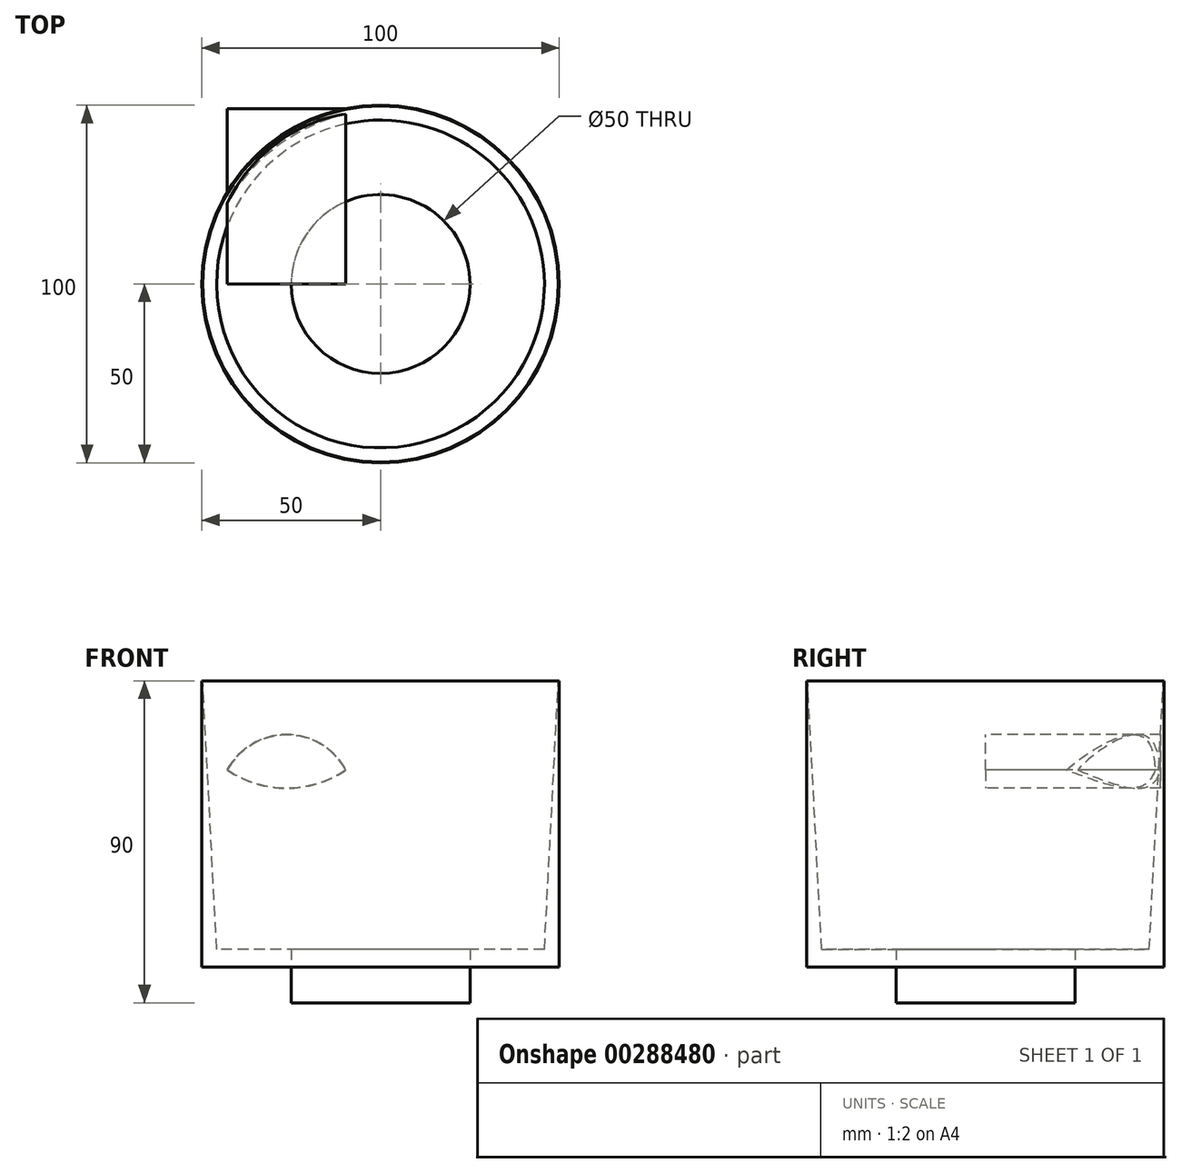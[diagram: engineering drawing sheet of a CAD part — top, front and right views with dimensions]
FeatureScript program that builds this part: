
annotation { "Feature Type Name" : "Feature", "Feature Type Description" : "" }
export const myFeature = defineFeature(function(context is Context, id is Id, definition is map)
    precondition{}
    {
        {
            var Q0;
            Q0=qCreatedBy(makeId("Top.planeOp"),FACE);
            var sketch = newSketch(context, id + "F0", { "sketchPlane" : qUnion([Q0])});
            skCircle(sketch, "E0", {"center": v(0, 0) * mm, "radius": 25 * mm});
            skSolve(sketch);
        }
        {
            var Q0;
            Q0=makeQuery(id+"F0.imprint","IMPRINT",FACE,{"disambiguationData":[TD([[makeQuery(id+"F0.imprint","IMPRINT",EDGE,{"derivedFrom":sQuery(id+"F0.wireOp",EDGE,"E0")}),1.0]])]});
            extrude(context, id + "F1", {"entities" : qUnion([Q0]), "depth" : 10 * mm});
        }
        {
            var Q0;
            Q0=makeQuery(id+"F1.opExtrude","CAP_FACE",FACE,{"disambiguationData":[OSD([sQuery(id+"F0.wireOp",EDGE,"E0")])],"isStart":false});
            var sketch = newSketch(context, id + "F2", { "sketchPlane" : qUnion([Q0])});
            skCircle(sketch, "E1", {"center": v(0, 0) * mm, "radius": 50 * mm});
            skSolve(sketch);
        }
        {
            var Q0;
            Q0=makeQuery(id+"F2.imprint","IMPRINT",FACE,{"disambiguationData":[TD([[makeQuery(id+"F2.imprint","IMPRINT",EDGE,{"derivedFrom":sQuery(id+"F2.wireOp",EDGE,"E1")}),1.0]])]});
            extrude(context, id + "F3", {"entities" : qUnion([Q0]), "depth" : 80 * mm});
        }
        {
            var Q0;
            Q0=makeQuery(id+"F3.opExtrude","CAP_FACE",FACE,{"disambiguationData":[OSD([sQuery(id+"F0.wireOp",EDGE,"E0"),sQuery(id+"F2.wireOp",EDGE,"E1")])],"isStart":false});
            var sketch = newSketch(context, id + "F4", { "sketchPlane" : qUnion([Q0])});
            skCircle(sketch, "E2", {"center": v(0, 0) * mm, "radius": 49.75 * mm});
            skSolve(sketch);
        }
        {
            var Q0;
            Q0 = qSketchRegion(id + "F4", true);
            extrude(context, id + "F5", {"entities" : qUnion([Q0]), "operationType" : NewBodyOperationType.REMOVE, "oppositeDirection" : true, "depth" : 75 * mm, "hasDraft" : true, "draftAngle" : 3 * degree, "draftPullDirection" : true});
        }
        {
            var Q0;
            Q0=qCreatedBy(makeId("Front.planeOp"),FACE);
            var sketch = newSketch(context, id + "F6", { "sketchPlane" : qUnion([Q0])});
            skArc(sketch, "E3", {"start": v(-42.83, 65.07) * mm, "mid": v(-26.27, 60) * mm, "end": v(-9.72, 65.07) * mm});
            skArc(sketch, "E4", {"start": v(-9.72, 65.07) * mm, "mid": v(-26.27, 75) * mm, "end": v(-42.83, 65.07) * mm});
            skSolve(sketch);
        }
        {
            var Q0;
            Q0 = qSketchRegion(id + "F6", true);
            extrude(context, id + "F7", {"entities" : qUnion([Q0]), "operationType" : NewBodyOperationType.ADD, "oppositeDirection" : true, "depth" : 49 * mm});
        }
    });
